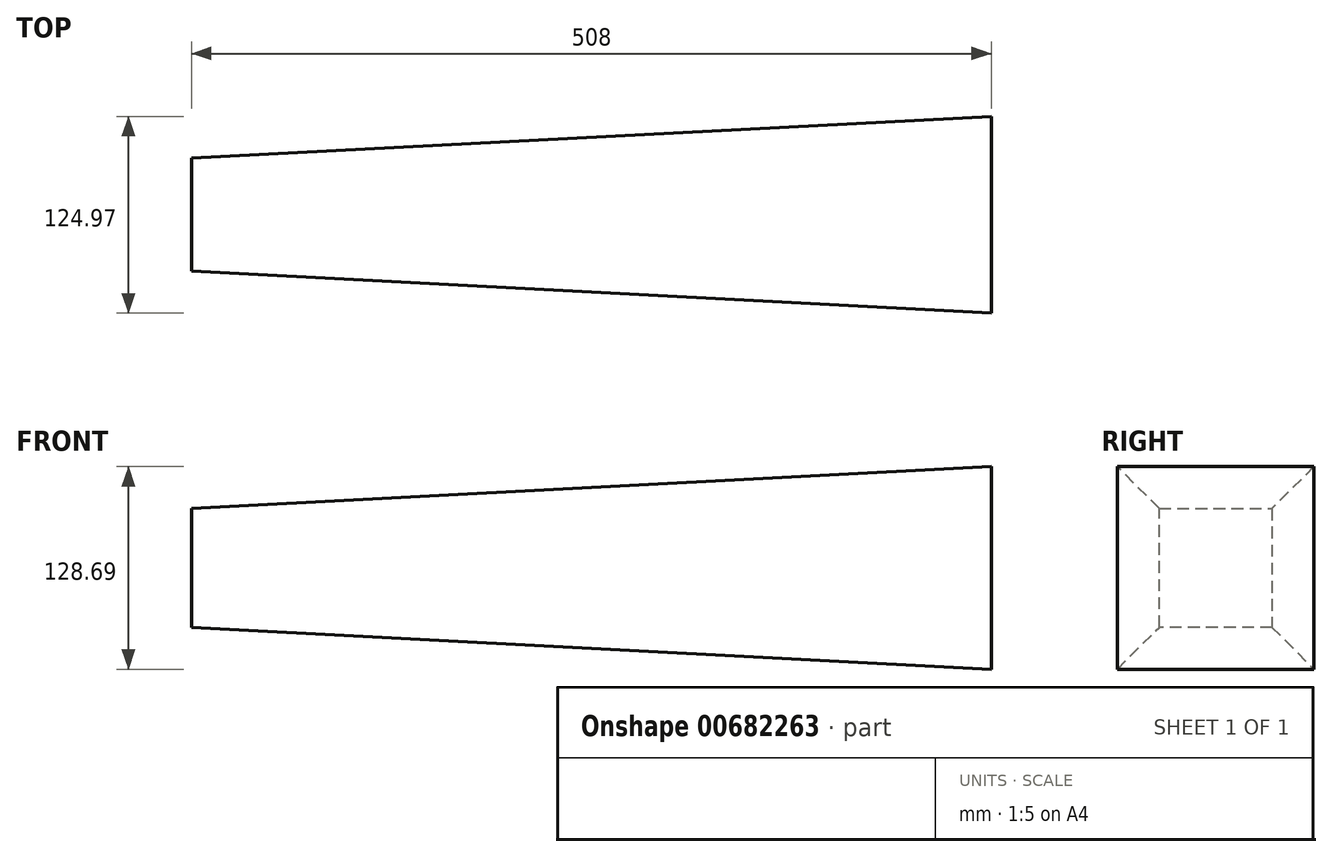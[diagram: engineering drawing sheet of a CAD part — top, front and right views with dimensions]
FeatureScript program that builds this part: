
annotation { "Feature Type Name" : "Feature", "Feature Type Description" : "" }
export const myFeature = defineFeature(function(context is Context, id is Id, definition is map)
    precondition{}
    {
        {
            var Q0;
            Q0=qCreatedBy(makeId("Right.planeOp"),FACE);
            var sketch = newSketch(context, id + "F0", { "sketchPlane" : qUnion([Q0])});
            skLineSegment(sketch, "E0.bottom", {"start": v(-45.9, 47.5) * mm, "end": v(25.82, 47.5) * mm});
            skLineSegment(sketch, "E0.top", {"start": v(-45.9, -27.95) * mm, "end": v(25.82, -27.95) * mm});
            skLineSegment(sketch, "E0.left", {"start": v(-45.9, 47.5) * mm, "end": v(-45.9, -27.95) * mm});
            skLineSegment(sketch, "E0.right", {"start": v(25.82, 47.5) * mm, "end": v(25.82, -27.95) * mm});
            skSolve(sketch);
        }
        {
            var Q0;
            Q0 = qSketchRegion(id + "F0", true);
            extrude(context, id + "F1", {"entities" : qUnion([Q0]), "depth" : 508 * mm, "offsetDistance" : 25.4 * mm, "hasDraft" : true, "draftAngle" : 3 * degree});
        }
    });
